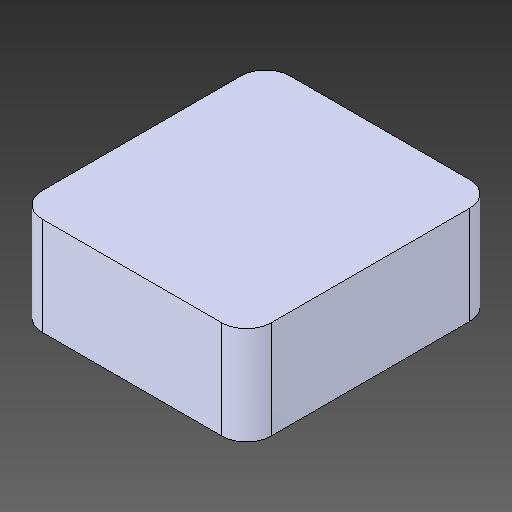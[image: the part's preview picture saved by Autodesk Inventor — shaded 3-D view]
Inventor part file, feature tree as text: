
AUTODESK INVENTOR PART (.ipt)
format: ipt  version: 2018.2 (Build 222227000, 227)  size: 84,992 bytes
history: native  units: mm
features: other x1, fillet x1
ambient origin geometry x8: Origin, YZ Plane, XZ Plane, XY Plane, X Axis, Y Axis, Z Axis, Center Point
bodies: Body1 (feature_tree)
feature tree (2):
  other  "ソリッド1"
  fillet  "Fillet1"  [1 undecoded]
note: 1 required parameter value undecoded (feature->parameter linkage not recoverable at this tier; creation-order binding heuristic only, values carry confidence <= 0.55)
